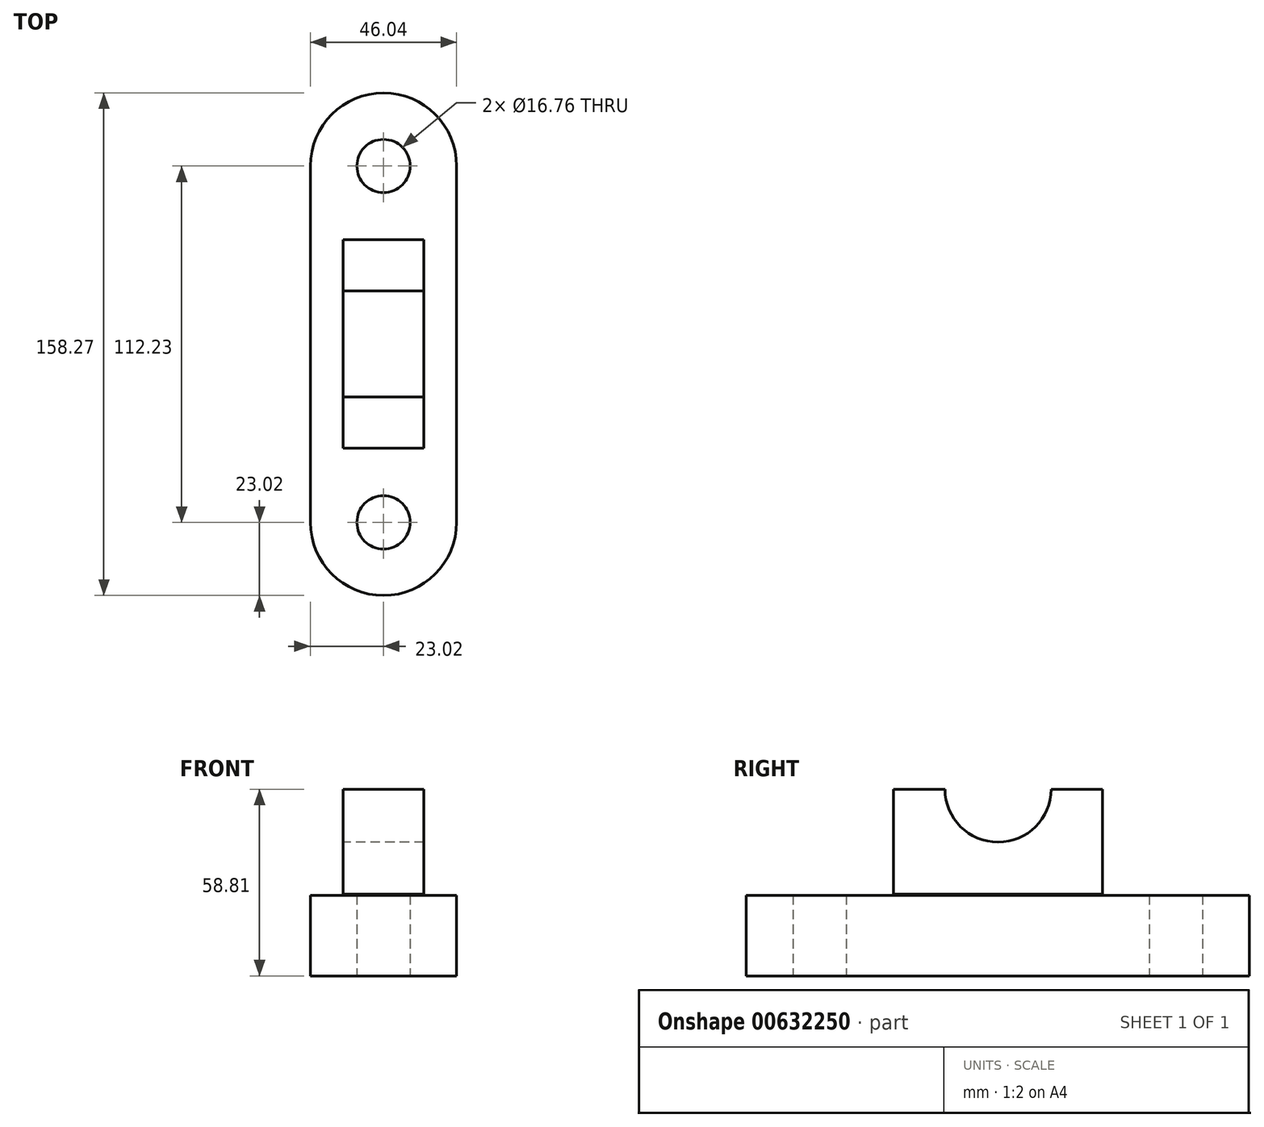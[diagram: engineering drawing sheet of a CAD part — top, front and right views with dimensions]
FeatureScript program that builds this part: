
annotation { "Feature Type Name" : "Feature", "Feature Type Description" : "" }
export const myFeature = defineFeature(function(context is Context, id is Id, definition is map)
    precondition{}
    {
        {
            var Q0;
            Q0=qCreatedBy(makeId("Top.planeOp"),FACE);
            var sketch = newSketch(context, id + "F0", { "sketchPlane" : qUnion([Q0])});
            skArc(sketch, "E0", {"start": v(23.02, 68.68) * mm, "mid": v(0, 91.7) * mm, "end": v(-23.02, 68.68) * mm});
            skArc(sketch, "E1", {"start": v(-23.02, -43.55) * mm, "mid": v(0, -66.57) * mm, "end": v(23.02, -43.55) * mm});
            skLineSegment(sketch, "E2", {"start": v(-23.02, 68.68) * mm, "end": v(-23.02, -43.55) * mm});
            skLineSegment(sketch, "E3", {"start": v(23.02, 68.68) * mm, "end": v(23.02, -43.55) * mm});
            skCircle(sketch, "E4", {"center": v(0, -43.55) * mm, "radius": 8.38 * mm});
            skCircle(sketch, "E5", {"center": v(0, 68.68) * mm, "radius": 8.38 * mm});
            skSolve(sketch);
        }
        {
            var Q0;
            Q0 = qSketchRegion(id + "F0", true);
            extrude(context, id + "F1", {"entities" : qUnion([Q0]), "depth" : 25.4 * mm, "offsetDistance" : 25.4 * mm});
        }
        {
            var Q0;
            Q0=qCreatedBy(makeId("Right.planeOp"),FACE);
            var sketch = newSketch(context, id + "F2", { "sketchPlane" : qUnion([Q0])});
            skLineSegment(sketch, "E6.bottom", {"start": v(45.53, 25.78) * mm, "end": v(-20.22, 25.78) * mm});
            skLineSegment(sketch, "E6.top", {"start": v(45.53, 58.8) * mm, "end": v(29.36, 58.8) * mm});
            skLineSegment(sketch, "E6.left", {"start": v(45.53, 25.78) * mm, "end": v(45.53, 58.8) * mm});
            skLineSegment(sketch, "E6.right", {"start": v(-20.22, 25.78) * mm, "end": v(-20.22, 58.8) * mm});
            skArc(sketch, "E7", {"start": v(-4.05, 58.8) * mm, "mid": v(12.66, 42.1) * mm, "end": v(29.36, 58.8) * mm});
            skLineSegment(sketch, "E8.trimOffspring", {"start": v(-4.05, 58.8) * mm, "end": v(-20.22, 58.8) * mm});
            skSolve(sketch);
        }
        {
            var Q0;
            Q0 = qSketchRegion(id + "F2", true);
            extrude(context, id + "F3", {"entities" : qUnion([Q0]), "endBound" : BoundingType.SYMMETRIC, "depth" : 25.4 * mm, "offsetDistance" : 25.4 * mm});
        }
    });
